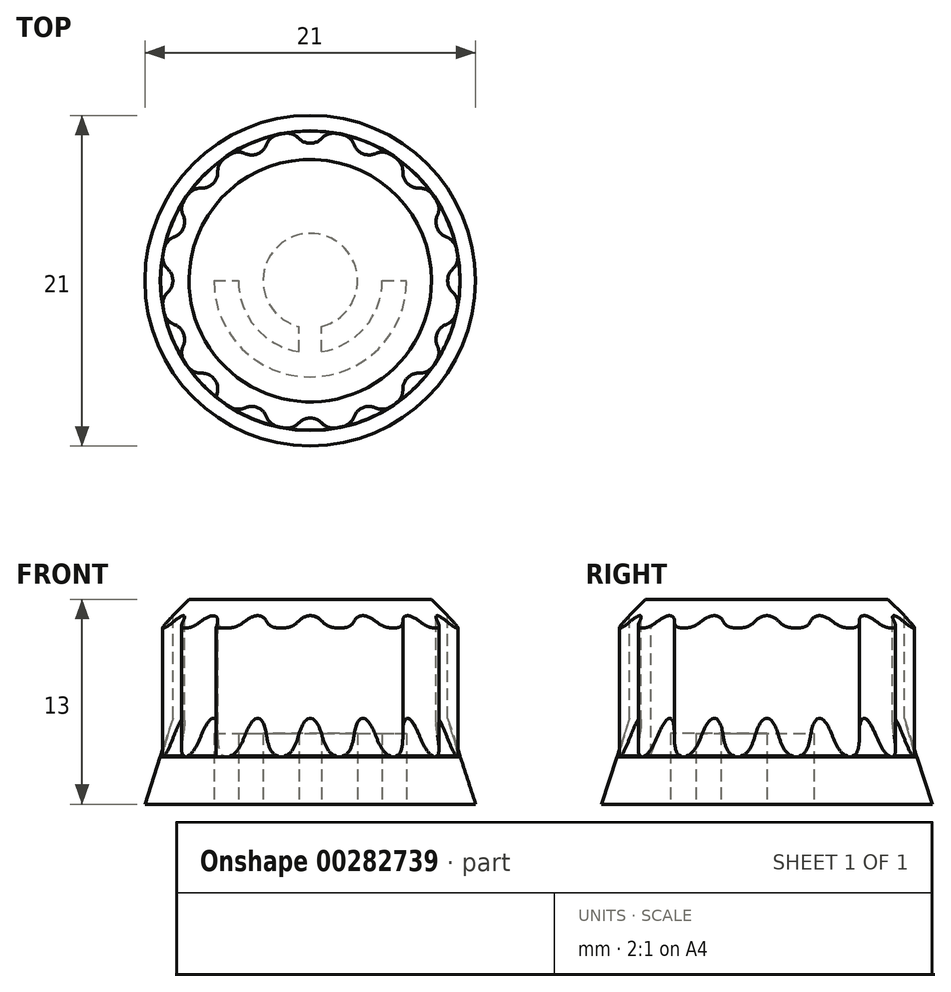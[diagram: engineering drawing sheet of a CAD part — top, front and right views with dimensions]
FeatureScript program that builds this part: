
annotation { "Feature Type Name" : "Feature", "Feature Type Description" : "" }
export const myFeature = defineFeature(function(context is Context, id is Id, definition is map)
    precondition{}
    {
        {
            var Q0;
            Q0=qCreatedBy(makeId("Top.planeOp"),FACE);
            var sketch = newSketch(context, id + "F0", { "sketchPlane" : qUnion([Q0])});
            skCircle(sketch, "E0", {"center": v(0, 0) * mm, "radius": 10.5 * mm});
            skSolve(sketch);
        }
        {
            var Q0;
            Q0=qCreatedBy(makeId("Top.planeOp"),FACE);
            cPlane(context, id + "F1", {"entities" : qUnion([Q0]), "cplaneType" : CPlaneType.OFFSET, "offset" : 12 * mm, "width" : 150 * mm, "height" : 150 * mm});
        }
        {
            var Q0;
            Q0=qCreatedBy(makeId("Top.planeOp"),FACE);
            cPlane(context, id + "F2", {"entities" : qUnion([Q0]), "cplaneType" : CPlaneType.OFFSET, "offset" : 3 * mm, "width" : 150 * mm, "height" : 150 * mm});
        }
        {
            var Q0;
            Q0=qCreatedBy(id+"F2.planeOp",FACE);
            var sketch = newSketch(context, id + "F3", { "sketchPlane" : qUnion([Q0])});
            skCircle(sketch, "E1", {"center": v(0, 0) * mm, "radius": 9.5 * mm});
            skSolve(sketch);
        }
        {
            var Q0;
            Q0 = qSketchRegion(id + "F0", true);
            extrude(context, id + "F4", {"entities" : qUnion([Q0]), "depth" : 3 * mm, "hasDraft" : true, "draftAngle" : 18 * degree, "draftPullDirection" : true});
        }
        {
            var Q0;
            Q0 = qSketchRegion(id + "F3", true);
            extrude(context, id + "F5", {"entities" : qUnion([Q0]), "operationType" : NewBodyOperationType.ADD, "depth" : 10 * mm});
        }
        {
            var Q0;
            Q0=qCreatedBy(id+"F1.planeOp",FACE);
            var sketch = newSketch(context, id + "F6", { "sketchPlane" : qUnion([Q0])});
            skArc(sketch, "E2", {"start": v(-1, 9.67) * mm, "mid": v(0, 8.73) * mm, "end": v(1, 9.67) * mm});
            skLineSegment(sketch, "E3", {"start": v(-1, 9.67) * mm, "end": v(1, 9.67) * mm});
            skSolve(sketch);
        }
        {
            var Q0;
            Q0 = qSketchRegion(id + "F6", true);
            var Q1;
            Q1=makeQuery(id+"F4.opExtrude","SWEPT_FACE",FACE,{"disambiguationData":[OSD([sQuery(id+"F0.wireOp",EDGE,"E0")])]});
            extrude(context, id + "F7", {"entities" : qUnion([Q0]), "endBound" : BoundingType.UP_TO_SURFACE, "oppositeDirection" : true, "endBoundEntityFace" : qUnion([Q1]), "depth" : 25 * mm});
        }
        {
            var Q0;
            Q0=makeQuery(id+"F7.opExtrude","SWEPT_BODY",BODY,{"disambiguationData":[OSD([sQuery(id+"F6.wireOp",EDGE,"E2"),sQuery(id+"F6.wireOp",EDGE,"E3")])]});
            var Q1;
            Q1=makeQuery(id+"F5.opExtrude","CAP_EDGE",EDGE,{"disambiguationData":[OSD([sQuery(id+"F3.wireOp",EDGE,"E1")])],"isStart":false});
            circularPattern(context, id + "F8", {"entities" : qUnion([Q0]), "axis" : qUnion([Q1]), "angle" : 360 * degree, "instanceCount" : 16, "equalSpace" : true});
        }
        {
            var Q0;
            Q0=makeQuery(id+"F7.opExtrude","SWEPT_BODY",BODY,{"disambiguationData":[OSD([sQuery(id+"F6.wireOp",EDGE,"E2"),sQuery(id+"F6.wireOp",EDGE,"E3")])]});
            var Q1;
            Q1=makeQuery(id+"F8.opPattern","COPY",BODY,{"derivedFrom":makeQuery(id+"F7.opExtrude","SWEPT_BODY",BODY,{"disambiguationData":[OSD([sQuery(id+"F6.wireOp",EDGE,"E2"),sQuery(id+"F6.wireOp",EDGE,"E3")])]}),"instanceName":"1"});
            var Q2;
            Q2=makeQuery(id+"F8.opPattern","COPY",BODY,{"derivedFrom":makeQuery(id+"F7.opExtrude","SWEPT_BODY",BODY,{"disambiguationData":[OSD([sQuery(id+"F6.wireOp",EDGE,"E2"),sQuery(id+"F6.wireOp",EDGE,"E3")])]}),"instanceName":"2"});
            var Q3;
            Q3=makeQuery(id+"F8.opPattern","COPY",BODY,{"derivedFrom":makeQuery(id+"F7.opExtrude","SWEPT_BODY",BODY,{"disambiguationData":[OSD([sQuery(id+"F6.wireOp",EDGE,"E2"),sQuery(id+"F6.wireOp",EDGE,"E3")])]}),"instanceName":"3"});
            var Q4;
            Q4=makeQuery(id+"F8.opPattern","COPY",BODY,{"derivedFrom":makeQuery(id+"F7.opExtrude","SWEPT_BODY",BODY,{"disambiguationData":[OSD([sQuery(id+"F6.wireOp",EDGE,"E2"),sQuery(id+"F6.wireOp",EDGE,"E3")])]}),"instanceName":"4"});
            var Q5;
            Q5=makeQuery(id+"F8.opPattern","COPY",BODY,{"derivedFrom":makeQuery(id+"F7.opExtrude","SWEPT_BODY",BODY,{"disambiguationData":[OSD([sQuery(id+"F6.wireOp",EDGE,"E2"),sQuery(id+"F6.wireOp",EDGE,"E3")])]}),"instanceName":"5"});
            var Q6;
            Q6=makeQuery(id+"F8.opPattern","COPY",BODY,{"derivedFrom":makeQuery(id+"F7.opExtrude","SWEPT_BODY",BODY,{"disambiguationData":[OSD([sQuery(id+"F6.wireOp",EDGE,"E2"),sQuery(id+"F6.wireOp",EDGE,"E3")])]}),"instanceName":"6"});
            var Q7;
            Q7=makeQuery(id+"F8.opPattern","COPY",BODY,{"derivedFrom":makeQuery(id+"F7.opExtrude","SWEPT_BODY",BODY,{"disambiguationData":[OSD([sQuery(id+"F6.wireOp",EDGE,"E2"),sQuery(id+"F6.wireOp",EDGE,"E3")])]}),"instanceName":"7"});
            var Q8;
            Q8=makeQuery(id+"F8.opPattern","COPY",BODY,{"derivedFrom":makeQuery(id+"F7.opExtrude","SWEPT_BODY",BODY,{"disambiguationData":[OSD([sQuery(id+"F6.wireOp",EDGE,"E2"),sQuery(id+"F6.wireOp",EDGE,"E3")])]}),"instanceName":"8"});
            var Q9;
            Q9=makeQuery(id+"F8.opPattern","COPY",BODY,{"derivedFrom":makeQuery(id+"F7.opExtrude","SWEPT_BODY",BODY,{"disambiguationData":[OSD([sQuery(id+"F6.wireOp",EDGE,"E2"),sQuery(id+"F6.wireOp",EDGE,"E3")])]}),"instanceName":"9"});
            var Q10;
            Q10=makeQuery(id+"F8.opPattern","COPY",BODY,{"derivedFrom":makeQuery(id+"F7.opExtrude","SWEPT_BODY",BODY,{"disambiguationData":[OSD([sQuery(id+"F6.wireOp",EDGE,"E2"),sQuery(id+"F6.wireOp",EDGE,"E3")])]}),"instanceName":"10"});
            var Q11;
            Q11=makeQuery(id+"F8.opPattern","COPY",BODY,{"derivedFrom":makeQuery(id+"F7.opExtrude","SWEPT_BODY",BODY,{"disambiguationData":[OSD([sQuery(id+"F6.wireOp",EDGE,"E2"),sQuery(id+"F6.wireOp",EDGE,"E3")])]}),"instanceName":"11"});
            var Q12;
            Q12=makeQuery(id+"F8.opPattern","COPY",BODY,{"derivedFrom":makeQuery(id+"F7.opExtrude","SWEPT_BODY",BODY,{"disambiguationData":[OSD([sQuery(id+"F6.wireOp",EDGE,"E2"),sQuery(id+"F6.wireOp",EDGE,"E3")])]}),"instanceName":"12"});
            var Q13;
            Q13=makeQuery(id+"F8.opPattern","COPY",BODY,{"derivedFrom":makeQuery(id+"F7.opExtrude","SWEPT_BODY",BODY,{"disambiguationData":[OSD([sQuery(id+"F6.wireOp",EDGE,"E2"),sQuery(id+"F6.wireOp",EDGE,"E3")])]}),"instanceName":"13"});
            var Q14;
            Q14=makeQuery(id+"F8.opPattern","COPY",BODY,{"derivedFrom":makeQuery(id+"F7.opExtrude","SWEPT_BODY",BODY,{"disambiguationData":[OSD([sQuery(id+"F6.wireOp",EDGE,"E2"),sQuery(id+"F6.wireOp",EDGE,"E3")])]}),"instanceName":"14"});
            var Q15;
            Q15=makeQuery(id+"F8.opPattern","COPY",BODY,{"derivedFrom":makeQuery(id+"F7.opExtrude","SWEPT_BODY",BODY,{"disambiguationData":[OSD([sQuery(id+"F6.wireOp",EDGE,"E2"),sQuery(id+"F6.wireOp",EDGE,"E3")])]}),"instanceName":"15"});
            var Q16;
            Q16=makeQuery(id+"F4.opExtrude","SWEPT_BODY",BODY,{"disambiguationData":[OSD([sQuery(id+"F0.wireOp",EDGE,"E0")])]});
            booleanBodies(context, id + "F9", {"operationType" : BooleanOperationType.SUBTRACTION, "tools" : qUnion([Q0, Q1, Q2, Q3, Q4, Q5, Q6, Q7, Q8, Q9, Q10, Q11, Q12, Q13, Q14, Q15]), "targets" : qUnion([Q16])});
        }
        {
            var Q0;
            Q0=makeQuery(id+"F9.opBoolean","INTERSECT",EDGE,{"disambiguationData":[OD(0.0)],"derivedFrom":[makeQuery(id+"F5.opExtrude","SWEPT_FACE",FACE,{"disambiguationData":[OSD([sQuery(id+"F3.wireOp",EDGE,"E1")])]}),makeQuery(id+"F8.opPattern","COPY",FACE,{"derivedFrom":makeQuery(id+"F7.opExtrude","SWEPT_FACE",FACE,{"disambiguationData":[OSD([sQuery(id+"F6.wireOp",EDGE,"E2")])]}),"instanceName":"15"})]});
            var Q1;
            Q1=makeQuery(id+"F9.opBoolean","INTERSECT",EDGE,{"disambiguationData":[OD(1.0)],"derivedFrom":[makeQuery(id+"F5.opExtrude","SWEPT_FACE",FACE,{"disambiguationData":[OSD([sQuery(id+"F3.wireOp",EDGE,"E1")])]}),makeQuery(id+"F8.opPattern","COPY",FACE,{"derivedFrom":makeQuery(id+"F7.opExtrude","SWEPT_FACE",FACE,{"disambiguationData":[OSD([sQuery(id+"F6.wireOp",EDGE,"E2")])]}),"instanceName":"15"})]});
            var Q2;
            Q2=makeQuery(id+"F9.opBoolean","INTERSECT",EDGE,{"disambiguationData":[OD(0.0)],"derivedFrom":[makeQuery(id+"F5.opExtrude","SWEPT_FACE",FACE,{"disambiguationData":[OSD([sQuery(id+"F3.wireOp",EDGE,"E1")])]}),makeQuery(id+"F8.opPattern","COPY",FACE,{"derivedFrom":makeQuery(id+"F7.opExtrude","SWEPT_FACE",FACE,{"disambiguationData":[OSD([sQuery(id+"F6.wireOp",EDGE,"E2")])]}),"instanceName":"14"})]});
            var Q3;
            Q3=makeQuery(id+"F9.opBoolean","INTERSECT",EDGE,{"disambiguationData":[OD(1.0)],"derivedFrom":[makeQuery(id+"F5.opExtrude","SWEPT_FACE",FACE,{"disambiguationData":[OSD([sQuery(id+"F3.wireOp",EDGE,"E1")])]}),makeQuery(id+"F8.opPattern","COPY",FACE,{"derivedFrom":makeQuery(id+"F7.opExtrude","SWEPT_FACE",FACE,{"disambiguationData":[OSD([sQuery(id+"F6.wireOp",EDGE,"E2")])]}),"instanceName":"14"})]});
            var Q4;
            Q4=makeQuery(id+"F9.opBoolean","INTERSECT",EDGE,{"disambiguationData":[OD(1.0)],"derivedFrom":[makeQuery(id+"F5.opExtrude","SWEPT_FACE",FACE,{"disambiguationData":[OSD([sQuery(id+"F3.wireOp",EDGE,"E1")])]}),makeQuery(id+"F8.opPattern","COPY",FACE,{"derivedFrom":makeQuery(id+"F7.opExtrude","SWEPT_FACE",FACE,{"disambiguationData":[OSD([sQuery(id+"F6.wireOp",EDGE,"E2")])]}),"instanceName":"13"})]});
            var Q5;
            Q5=makeQuery(id+"F9.opBoolean","INTERSECT",EDGE,{"disambiguationData":[OD(0.0)],"derivedFrom":[makeQuery(id+"F5.opExtrude","SWEPT_FACE",FACE,{"disambiguationData":[OSD([sQuery(id+"F3.wireOp",EDGE,"E1")])]}),makeQuery(id+"F8.opPattern","COPY",FACE,{"derivedFrom":makeQuery(id+"F7.opExtrude","SWEPT_FACE",FACE,{"disambiguationData":[OSD([sQuery(id+"F6.wireOp",EDGE,"E2")])]}),"instanceName":"13"})]});
            var Q6;
            Q6=makeQuery(id+"F9.opBoolean","INTERSECT",EDGE,{"disambiguationData":[OD(1.0)],"derivedFrom":[makeQuery(id+"F5.opExtrude","SWEPT_FACE",FACE,{"disambiguationData":[OSD([sQuery(id+"F3.wireOp",EDGE,"E1")])]}),makeQuery(id+"F8.opPattern","COPY",FACE,{"derivedFrom":makeQuery(id+"F7.opExtrude","SWEPT_FACE",FACE,{"disambiguationData":[OSD([sQuery(id+"F6.wireOp",EDGE,"E2")])]}),"instanceName":"12"})]});
            var Q7;
            Q7=makeQuery(id+"F9.opBoolean","INTERSECT",EDGE,{"disambiguationData":[OD(0.0)],"derivedFrom":[makeQuery(id+"F5.opExtrude","SWEPT_FACE",FACE,{"disambiguationData":[OSD([sQuery(id+"F3.wireOp",EDGE,"E1")])]}),makeQuery(id+"F8.opPattern","COPY",FACE,{"derivedFrom":makeQuery(id+"F7.opExtrude","SWEPT_FACE",FACE,{"disambiguationData":[OSD([sQuery(id+"F6.wireOp",EDGE,"E2")])]}),"instanceName":"12"})]});
            var Q8;
            Q8=makeQuery(id+"F9.opBoolean","INTERSECT",EDGE,{"disambiguationData":[OD(1.0)],"derivedFrom":[makeQuery(id+"F5.opExtrude","SWEPT_FACE",FACE,{"disambiguationData":[OSD([sQuery(id+"F3.wireOp",EDGE,"E1")])]}),makeQuery(id+"F8.opPattern","COPY",FACE,{"derivedFrom":makeQuery(id+"F7.opExtrude","SWEPT_FACE",FACE,{"disambiguationData":[OSD([sQuery(id+"F6.wireOp",EDGE,"E2")])]}),"instanceName":"11"})]});
            var Q9;
            Q9=makeQuery(id+"F9.opBoolean","INTERSECT",EDGE,{"disambiguationData":[OD(0.0)],"derivedFrom":[makeQuery(id+"F5.opExtrude","SWEPT_FACE",FACE,{"disambiguationData":[OSD([sQuery(id+"F3.wireOp",EDGE,"E1")])]}),makeQuery(id+"F8.opPattern","COPY",FACE,{"derivedFrom":makeQuery(id+"F7.opExtrude","SWEPT_FACE",FACE,{"disambiguationData":[OSD([sQuery(id+"F6.wireOp",EDGE,"E2")])]}),"instanceName":"11"})]});
            var Q10;
            Q10=makeQuery(id+"F9.opBoolean","INTERSECT",EDGE,{"disambiguationData":[OD(1.0)],"derivedFrom":[makeQuery(id+"F5.opExtrude","SWEPT_FACE",FACE,{"disambiguationData":[OSD([sQuery(id+"F3.wireOp",EDGE,"E1")])]}),makeQuery(id+"F8.opPattern","COPY",FACE,{"derivedFrom":makeQuery(id+"F7.opExtrude","SWEPT_FACE",FACE,{"disambiguationData":[OSD([sQuery(id+"F6.wireOp",EDGE,"E2")])]}),"instanceName":"10"})]});
            var Q11;
            Q11=makeQuery(id+"F9.opBoolean","INTERSECT",EDGE,{"disambiguationData":[OD(0.0)],"derivedFrom":[makeQuery(id+"F5.opExtrude","SWEPT_FACE",FACE,{"disambiguationData":[OSD([sQuery(id+"F3.wireOp",EDGE,"E1")])]}),makeQuery(id+"F8.opPattern","COPY",FACE,{"derivedFrom":makeQuery(id+"F7.opExtrude","SWEPT_FACE",FACE,{"disambiguationData":[OSD([sQuery(id+"F6.wireOp",EDGE,"E2")])]}),"instanceName":"10"})]});
            var Q12;
            Q12=makeQuery(id+"F9.opBoolean","INTERSECT",EDGE,{"disambiguationData":[OD(1.0)],"derivedFrom":[makeQuery(id+"F5.opExtrude","SWEPT_FACE",FACE,{"disambiguationData":[OSD([sQuery(id+"F3.wireOp",EDGE,"E1")])]}),makeQuery(id+"F8.opPattern","COPY",FACE,{"derivedFrom":makeQuery(id+"F7.opExtrude","SWEPT_FACE",FACE,{"disambiguationData":[OSD([sQuery(id+"F6.wireOp",EDGE,"E2")])]}),"instanceName":"9"})]});
            var Q13;
            Q13=makeQuery(id+"F9.opBoolean","INTERSECT",EDGE,{"disambiguationData":[OD(0.0)],"derivedFrom":[makeQuery(id+"F5.opExtrude","SWEPT_FACE",FACE,{"disambiguationData":[OSD([sQuery(id+"F3.wireOp",EDGE,"E1")])]}),makeQuery(id+"F8.opPattern","COPY",FACE,{"derivedFrom":makeQuery(id+"F7.opExtrude","SWEPT_FACE",FACE,{"disambiguationData":[OSD([sQuery(id+"F6.wireOp",EDGE,"E2")])]}),"instanceName":"9"})]});
            var Q14;
            Q14=makeQuery(id+"F9.opBoolean","INTERSECT",EDGE,{"disambiguationData":[OD(1.0)],"derivedFrom":[makeQuery(id+"F5.opExtrude","SWEPT_FACE",FACE,{"disambiguationData":[OSD([sQuery(id+"F3.wireOp",EDGE,"E1")])]}),makeQuery(id+"F8.opPattern","COPY",FACE,{"derivedFrom":makeQuery(id+"F7.opExtrude","SWEPT_FACE",FACE,{"disambiguationData":[OSD([sQuery(id+"F6.wireOp",EDGE,"E2")])]}),"instanceName":"8"})]});
            var Q15;
            Q15=makeQuery(id+"F9.opBoolean","INTERSECT",EDGE,{"disambiguationData":[OD(0.0)],"derivedFrom":[makeQuery(id+"F5.opExtrude","SWEPT_FACE",FACE,{"disambiguationData":[OSD([sQuery(id+"F3.wireOp",EDGE,"E1")])]}),makeQuery(id+"F8.opPattern","COPY",FACE,{"derivedFrom":makeQuery(id+"F7.opExtrude","SWEPT_FACE",FACE,{"disambiguationData":[OSD([sQuery(id+"F6.wireOp",EDGE,"E2")])]}),"instanceName":"8"})]});
            var Q16;
            Q16=makeQuery(id+"F9.opBoolean","INTERSECT",EDGE,{"disambiguationData":[OD(1.0)],"derivedFrom":[makeQuery(id+"F5.opExtrude","SWEPT_FACE",FACE,{"disambiguationData":[OSD([sQuery(id+"F3.wireOp",EDGE,"E1")])]}),makeQuery(id+"F8.opPattern","COPY",FACE,{"derivedFrom":makeQuery(id+"F7.opExtrude","SWEPT_FACE",FACE,{"disambiguationData":[OSD([sQuery(id+"F6.wireOp",EDGE,"E2")])]}),"instanceName":"7"})]});
            var Q17;
            Q17=makeQuery(id+"F9.opBoolean","INTERSECT",EDGE,{"disambiguationData":[OD(0.0)],"derivedFrom":[makeQuery(id+"F5.opExtrude","SWEPT_FACE",FACE,{"disambiguationData":[OSD([sQuery(id+"F3.wireOp",EDGE,"E1")])]}),makeQuery(id+"F8.opPattern","COPY",FACE,{"derivedFrom":makeQuery(id+"F7.opExtrude","SWEPT_FACE",FACE,{"disambiguationData":[OSD([sQuery(id+"F6.wireOp",EDGE,"E2")])]}),"instanceName":"7"})]});
            var Q18;
            Q18=makeQuery(id+"F9.opBoolean","INTERSECT",EDGE,{"disambiguationData":[OD(0.0)],"derivedFrom":[makeQuery(id+"F5.opExtrude","SWEPT_FACE",FACE,{"disambiguationData":[OSD([sQuery(id+"F3.wireOp",EDGE,"E1")])]}),makeQuery(id+"F8.opPattern","COPY",FACE,{"derivedFrom":makeQuery(id+"F7.opExtrude","SWEPT_FACE",FACE,{"disambiguationData":[OSD([sQuery(id+"F6.wireOp",EDGE,"E2")])]}),"instanceName":"6"})]});
            var Q19;
            Q19=makeQuery(id+"F9.opBoolean","INTERSECT",EDGE,{"disambiguationData":[OD(0.0)],"derivedFrom":[makeQuery(id+"F5.opExtrude","SWEPT_FACE",FACE,{"disambiguationData":[OSD([sQuery(id+"F3.wireOp",EDGE,"E1")])]}),makeQuery(id+"F8.opPattern","COPY",FACE,{"derivedFrom":makeQuery(id+"F7.opExtrude","SWEPT_FACE",FACE,{"disambiguationData":[OSD([sQuery(id+"F6.wireOp",EDGE,"E2")])]}),"instanceName":"5"})]});
            var Q20;
            Q20=makeQuery(id+"F9.opBoolean","INTERSECT",EDGE,{"disambiguationData":[OD(1.0)],"derivedFrom":[makeQuery(id+"F5.opExtrude","SWEPT_FACE",FACE,{"disambiguationData":[OSD([sQuery(id+"F3.wireOp",EDGE,"E1")])]}),makeQuery(id+"F8.opPattern","COPY",FACE,{"derivedFrom":makeQuery(id+"F7.opExtrude","SWEPT_FACE",FACE,{"disambiguationData":[OSD([sQuery(id+"F6.wireOp",EDGE,"E2")])]}),"instanceName":"5"})]});
            var Q21;
            Q21=makeQuery(id+"F9.opBoolean","INTERSECT",EDGE,{"disambiguationData":[OD(0.0)],"derivedFrom":[makeQuery(id+"F5.opExtrude","SWEPT_FACE",FACE,{"disambiguationData":[OSD([sQuery(id+"F3.wireOp",EDGE,"E1")])]}),makeQuery(id+"F8.opPattern","COPY",FACE,{"derivedFrom":makeQuery(id+"F7.opExtrude","SWEPT_FACE",FACE,{"disambiguationData":[OSD([sQuery(id+"F6.wireOp",EDGE,"E2")])]}),"instanceName":"4"})]});
            var Q22;
            Q22=makeQuery(id+"F9.opBoolean","INTERSECT",EDGE,{"disambiguationData":[OD(1.0)],"derivedFrom":[makeQuery(id+"F5.opExtrude","SWEPT_FACE",FACE,{"disambiguationData":[OSD([sQuery(id+"F3.wireOp",EDGE,"E1")])]}),makeQuery(id+"F8.opPattern","COPY",FACE,{"derivedFrom":makeQuery(id+"F7.opExtrude","SWEPT_FACE",FACE,{"disambiguationData":[OSD([sQuery(id+"F6.wireOp",EDGE,"E2")])]}),"instanceName":"4"})]});
            var Q23;
            Q23=makeQuery(id+"F9.opBoolean","INTERSECT",EDGE,{"disambiguationData":[OD(0.0)],"derivedFrom":[makeQuery(id+"F5.opExtrude","SWEPT_FACE",FACE,{"disambiguationData":[OSD([sQuery(id+"F3.wireOp",EDGE,"E1")])]}),makeQuery(id+"F8.opPattern","COPY",FACE,{"derivedFrom":makeQuery(id+"F7.opExtrude","SWEPT_FACE",FACE,{"disambiguationData":[OSD([sQuery(id+"F6.wireOp",EDGE,"E2")])]}),"instanceName":"3"})]});
            var Q24;
            Q24=makeQuery(id+"F9.opBoolean","INTERSECT",EDGE,{"disambiguationData":[OD(1.0)],"derivedFrom":[makeQuery(id+"F5.opExtrude","SWEPT_FACE",FACE,{"disambiguationData":[OSD([sQuery(id+"F3.wireOp",EDGE,"E1")])]}),makeQuery(id+"F8.opPattern","COPY",FACE,{"derivedFrom":makeQuery(id+"F7.opExtrude","SWEPT_FACE",FACE,{"disambiguationData":[OSD([sQuery(id+"F6.wireOp",EDGE,"E2")])]}),"instanceName":"3"})]});
            var Q25;
            Q25=makeQuery(id+"F9.opBoolean","INTERSECT",EDGE,{"disambiguationData":[OD(0.0)],"derivedFrom":[makeQuery(id+"F5.opExtrude","SWEPT_FACE",FACE,{"disambiguationData":[OSD([sQuery(id+"F3.wireOp",EDGE,"E1")])]}),makeQuery(id+"F8.opPattern","COPY",FACE,{"derivedFrom":makeQuery(id+"F7.opExtrude","SWEPT_FACE",FACE,{"disambiguationData":[OSD([sQuery(id+"F6.wireOp",EDGE,"E2")])]}),"instanceName":"2"})]});
            var Q26;
            Q26=makeQuery(id+"F9.opBoolean","INTERSECT",EDGE,{"disambiguationData":[OD(1.0)],"derivedFrom":[makeQuery(id+"F5.opExtrude","SWEPT_FACE",FACE,{"disambiguationData":[OSD([sQuery(id+"F3.wireOp",EDGE,"E1")])]}),makeQuery(id+"F8.opPattern","COPY",FACE,{"derivedFrom":makeQuery(id+"F7.opExtrude","SWEPT_FACE",FACE,{"disambiguationData":[OSD([sQuery(id+"F6.wireOp",EDGE,"E2")])]}),"instanceName":"2"})]});
            var Q27;
            Q27=makeQuery(id+"F9.opBoolean","INTERSECT",EDGE,{"disambiguationData":[OD(0.0)],"derivedFrom":[makeQuery(id+"F5.opExtrude","SWEPT_FACE",FACE,{"disambiguationData":[OSD([sQuery(id+"F3.wireOp",EDGE,"E1")])]}),makeQuery(id+"F8.opPattern","COPY",FACE,{"derivedFrom":makeQuery(id+"F7.opExtrude","SWEPT_FACE",FACE,{"disambiguationData":[OSD([sQuery(id+"F6.wireOp",EDGE,"E2")])]}),"instanceName":"1"})]});
            var Q28;
            Q28=makeQuery(id+"F9.opBoolean","INTERSECT",EDGE,{"disambiguationData":[OD(1.0)],"derivedFrom":[makeQuery(id+"F5.opExtrude","SWEPT_FACE",FACE,{"disambiguationData":[OSD([sQuery(id+"F3.wireOp",EDGE,"E1")])]}),makeQuery(id+"F8.opPattern","COPY",FACE,{"derivedFrom":makeQuery(id+"F7.opExtrude","SWEPT_FACE",FACE,{"disambiguationData":[OSD([sQuery(id+"F6.wireOp",EDGE,"E2")])]}),"instanceName":"1"})]});
            var Q29;
            Q29=makeQuery(id+"F9.opBoolean","INTERSECT",EDGE,{"disambiguationData":[OD(0.0)],"derivedFrom":[makeQuery(id+"F5.opExtrude","SWEPT_FACE",FACE,{"disambiguationData":[OSD([sQuery(id+"F3.wireOp",EDGE,"E1")])]}),makeQuery(id+"F7.opExtrude","SWEPT_FACE",FACE,{"disambiguationData":[OSD([sQuery(id+"F6.wireOp",EDGE,"E2")])]})]});
            var Q30;
            Q30=makeQuery(id+"F9.opBoolean","INTERSECT",EDGE,{"disambiguationData":[OD(1.0)],"derivedFrom":[makeQuery(id+"F5.opExtrude","SWEPT_FACE",FACE,{"disambiguationData":[OSD([sQuery(id+"F3.wireOp",EDGE,"E1")])]}),makeQuery(id+"F7.opExtrude","SWEPT_FACE",FACE,{"disambiguationData":[OSD([sQuery(id+"F6.wireOp",EDGE,"E2")])]})]});
            fillet(context, id + "F10", {"entities" : qUnion([Q0, Q1, Q2, Q3, Q4, Q5, Q6, Q7, Q8, Q9, Q10, Q11, Q12, Q13, Q14, Q15, Q16, Q17, Q18, Q19, Q20, Q21, Q22, Q23, Q24, Q25, Q26, Q27, Q28, Q29, Q30]), "radius" : 1 * mm, "tangentPropagation" : true, "allowEdgeOverflow" : false});
        }
        {
            var Q0;
            Q0=makeQuery(id+"F5.opExtrude","CAP_EDGE",EDGE,{"disambiguationData":[OSD([sQuery(id+"F3.wireOp",EDGE,"E1")])],"isStart":false});
            chamfer(context, id + "F11", {"entities" : qUnion([Q0]), "width" : 1.8 * mm, "tangentPropagation" : true});
        }
        {
            var Q0;
            Q0=qCreatedBy(makeId("Top.planeOp"),FACE);
            var sketch = newSketch(context, id + "F12", { "sketchPlane" : qUnion([Q0])});
            skArc(sketch, "E4", {"start": v(-6.12, 0) * mm, "mid": v(0, -6.12) * mm, "end": v(6.12, 0) * mm});
            skLineSegment(sketch, "E5", {"start": v(-6.12, 0) * mm, "end": v(-4.57, 0) * mm});
            skLineSegment(sketch, "E6", {"start": v(4.57, 0) * mm, "end": v(6.12, 0) * mm});
            skLineSegment(sketch, "E7", {"start": v(-0.72, -4.51) * mm, "end": v(-0.72, -2.91) * mm});
            skLineSegment(sketch, "E8", {"start": v(0.72, -4.51) * mm, "end": v(0.72, -2.91) * mm});
            skArc(sketch, "E9", {"start": v(0.72, -2.91) * mm, "mid": v(0, 3) * mm, "end": v(-0.72, -2.91) * mm});
            skArc(sketch, "E10", {"start": v(0.72, -4.51) * mm, "mid": v(3.48, -2.97) * mm, "end": v(4.57, 0) * mm});
            skArc(sketch, "E11", {"start": v(-4.57, 0) * mm, "mid": v(-3.48, -2.97) * mm, "end": v(-0.72, -4.51) * mm});
            skSolve(sketch);
        }
        {
            var Q0;
            Q0 = qSketchRegion(id + "F12", true);
            extrude(context, id + "F13", {"entities" : qUnion([Q0]), "operationType" : NewBodyOperationType.REMOVE, "depth" : 4.5 * mm});
        }
    });
